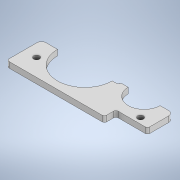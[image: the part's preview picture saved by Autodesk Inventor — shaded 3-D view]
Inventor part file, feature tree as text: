
AUTODESK INVENTOR PART (.ipt)
format: ipt  version: 2021 (Build 250183000, 183)  size: 215,552 bytes
history: native  units: mm
features: sketch x5, extrude x4, fillet x2, projected_geometry x2, hole x1
ambient origin geometry x8: Origin, YZ Plane, XZ Plane, XY Plane, X Axis, Y Axis, Z Axis, Center Point
bodies: Solid1 (feature_tree)
feature tree (14):
  extrude  "Extrusion1"  Depth=56.25mm
  sketch  "Sketch2"  dims[d16=58.25mm d17=116.5mm]
  sketch  "Sketch3"  dims[d18=112.5mm d19=18.5mm]
  extrude  "Extrusion2"  Depth=116.5mm
  extrude  "Extrusion3"  Depth=112.5mm
  extrude  "Extrusion4"  Depth=5.0mm TaperAngle=0.0deg
  hole  "Hole1"  [1 undecoded]
  fillet  "Fillet1"  Radius=2.0mm
  fillet  "Fillet2"  Radius=35.0mm
  sketch  "Sketch1"  dims[d0=47.7mm d1=27.7mm d2=27.7mm d3=27.7mm d4=27.7mm d7=37.0mm d9=30.9mm d10=19.5mm d11=35.0mm d12=35.0mm d13=25.8mm d14=28.0mm d15=56.25mm]
  projected_geometry  "Projected Loop1"
  projected_geometry  "Projected Loop2"
  sketch  "Sketch4"  dims[d20=32.45mm d21=5.0mm d22=0.0mm]
  sketch  "Sketch5"  dims[d23=74.0mm d25=38.5mm d26=2.0mm d27=35.0mm d28=19.5mm d29=67.0mm d30=2.0mm d31=0.0mm d32=0.0mm d33=10.0mm d34=0.0mm d35=27.5mm d36=10.0mm d37=2.0mm d38=0.0mm d39=0.0mm d40=11.0mm d41=11.0mm d42=15.0mm d43=15.0mm d44=11.0mm d45=7.0mm d46=11.0mm d47=7.0mm d48=6.0mm d49=3.5mm d50=6.0mm d51=3.5mm d52=5.1mm d53=6.0mm d54=4.0mm d55=2.0mm d56=90.0deg d57=8.0mm d58=20.594885mm d59=4.0mm d60=2.0mm]
note: 1 required parameter value undecoded (feature->parameter linkage not recoverable at this tier; creation-order binding heuristic only, values carry confidence <= 0.55)
